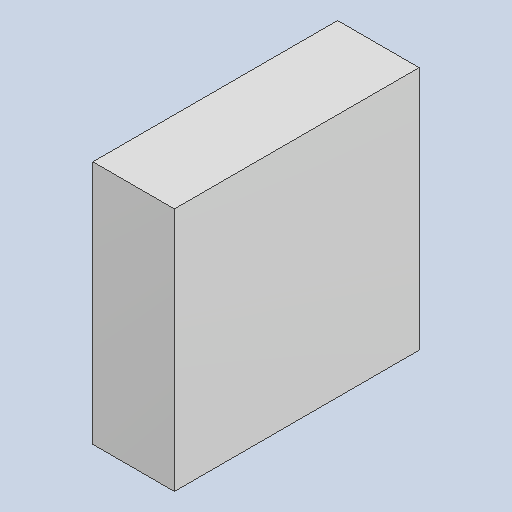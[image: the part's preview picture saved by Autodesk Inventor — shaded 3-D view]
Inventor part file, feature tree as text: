
AUTODESK INVENTOR PART (.ipt)
format: ipt  version: 2023.4 (Build 274418000, 418)  size: 81,408 bytes
history: native  units: mm
features: extrude x1
ambient origin geometry x8: Origin, YZ Plane, XZ Plane, XY Plane, X Axis, Y Axis, Z Axis, Center Point
bodies: Solid1 (feature_tree)
feature tree (1):
  extrude  "Extruded_22"  [1 undecoded]
note: 1 required parameter value undecoded (feature->parameter linkage not recoverable at this tier; creation-order binding heuristic only, values carry confidence <= 0.55)
